# Revit family: 707630001_Valvula Compuerta 1-2P
name_source: partatom
category: Pipe Accessories
units: mm (PartAtom-declared; Revit-internal decimal feet)

## family parameters
Always vertical = Yes
Cut with Voids When Loaded = No
OmniClass Number = 23.27.31.13.11
OmniClass Title = Gate Balancing Valves
Part Type = Valve - Normal
Round Connector Dimension = Use Diameter
Shared = No
Work Plane-Based = No

## types (3) — shared parameters
Creado por = BIMBAU
Cuidado Y Limpieza = Limpiar con un paño húmedo.-No se debe limpiar con elementos abrasivos como esponjas de alambre, ácidos o disolventes.
Description = Manĳa que facilita su operación.-Nuevo diseño robusto y resistente.-Válvula para trabajo pesado (145 psi).-Diseñadas y fabricadas para garantizar una larga vida útil.
Fecha de creación = 16/03/2021
Funcionalidad a presion de trabajo = 225 psi
Manufacturer = Grival
Presion maxima = 290 psi.
Presion minima = 20 psi.
Recubrimientos = Natural
Temperatura de uso = 82ºC - 179,6ºF
URL = https://www.grival.com
Vida útil = 5,000 ciclos.
zero-valued in all types: Default Elevation

## per-type parameters (varying)
| type | Alto | Diametro 2 | Diámetro | Longitud | Peso  Bruto | Peso neto | Referencia | Rosca de tubería |
| Válvula Compuerta 1" | 75.7 mm  [stored 0.24836 ft] | 57.5 mm  [stored 0.188648 ft] | 25.4 mm  [stored 0.0833333 ft] | 45 mm  [stored 0.147638 ft] | 454 gr. - 1 lb. | 445 gr. - 0,98 lb. | 707650001 | Galga de 1” 11-1/2 NPT |
| Válvula Compuerta 1/2" | 61.5 mm  [stored 0.201772 ft] | 53 mm  [stored 0.173885 ft] | 12.7 mm  [stored 0.0416667 ft] | 38 mm  [stored 0.124672 ft] | 191 gr. - 0,42 lb. | 185 gr. - 0,40 lb. | 707630001 | Galga de 1/2” 14 NPT GF30866 |
| Válvula Compuerta 3/4" | 69 mm  [stored 0.226378 ft] | 53 mm  [stored 0.173885 ft] | 19.05 mm  [stored 0.0625 ft] | 41 mm  [stored 0.134514 ft] | 207 gr. - 0,45 lb. | 200 gr. - 0,44 lb. | 707640001 | Galga de 3/4” 14 NPT |

note: column(s) folded — value = type name in every type: Model

type visibility flags: 3 boolean params named "<type name>" — each type sets only its own to Yes (folded from table)

note: [stored X ft] marks values corroborated as IEEE doubles in the binary element streams (Revit-internal decimal feet)

## geometry (parser evidence)
native form markers: Sweep x7
no freeform markers — native parametric forms only
